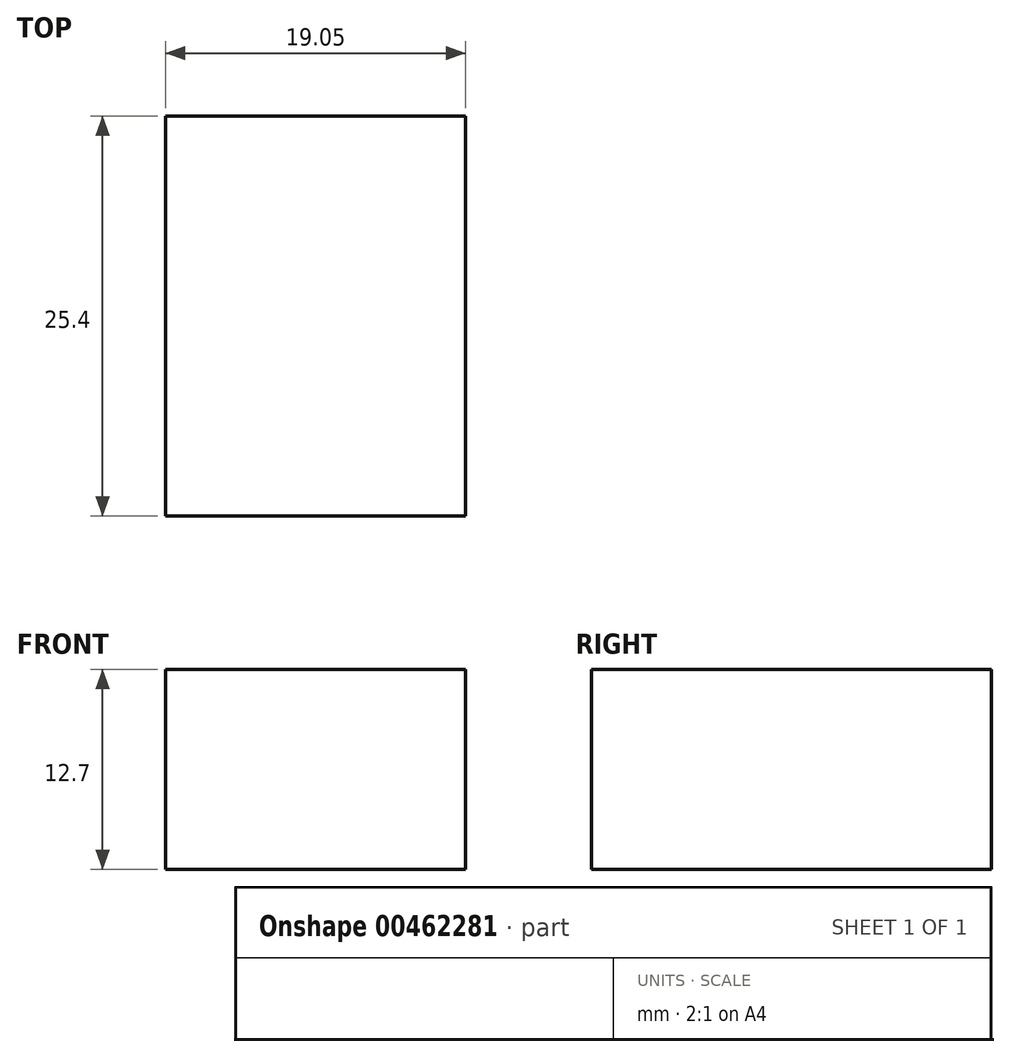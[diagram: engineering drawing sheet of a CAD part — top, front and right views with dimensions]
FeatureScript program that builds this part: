
annotation { "Feature Type Name" : "Feature", "Feature Type Description" : "" }
export const myFeature = defineFeature(function(context is Context, id is Id, definition is map)
    precondition{}
    {
        {
            var Q0;
            Q0=qCreatedBy(makeId("Front.planeOp"),FACE);
            var sketch = newSketch(context, id + "F0", { "sketchPlane" : qUnion([Q0])});
            skLineSegment(sketch, "E0.bottom", {"start": v(-50.8, 25.4) * mm, "end": v(50.8, 25.4) * mm});
            skLineSegment(sketch, "E0.top", {"start": v(-50.8, -25.4) * mm, "end": v(50.8, -25.4) * mm});
            skLineSegment(sketch, "E0.left", {"start": v(-50.8, 25.4) * mm, "end": v(-50.8, -25.4) * mm});
            skLineSegment(sketch, "E0.right", {"start": v(50.8, 25.4) * mm, "end": v(50.8, -25.4) * mm});
            skPoint(sketch, "E0.middle", {"position": v(0, 0) * mm});
            skLineSegment(sketch, "E1.bottom", {"start": v(31.75, -25.4) * mm, "end": v(50.8, -25.4) * mm});
            skLineSegment(sketch, "E1.top", {"start": v(31.75, -12.7) * mm, "end": v(50.8, -12.7) * mm});
            skLineSegment(sketch, "E1.left", {"start": v(31.75, -25.4) * mm, "end": v(31.75, -12.7) * mm});
            skLineSegment(sketch, "E1.right", {"start": v(50.8, -25.4) * mm, "end": v(50.8, -12.7) * mm});
            skLineSegment(sketch, "E2.bottom", {"start": v(-23.76, 25.4) * mm, "end": v(27.04, 25.4) * mm});
            skLineSegment(sketch, "E2.top", {"start": v(-23.76, 12.7) * mm, "end": v(27.04, 12.7) * mm});
            skLineSegment(sketch, "E2.left", {"start": v(-23.76, 25.4) * mm, "end": v(-23.76, 12.7) * mm});
            skLineSegment(sketch, "E2.right", {"start": v(27.04, 25.4) * mm, "end": v(27.04, 12.7) * mm});
            skSolve(sketch);
        }
        {
            var Q0;
            Q0=makeQuery(id+"F0.imprint","IMPRINT",FACE,{"disambiguationData":[TD([[makeQuery(id+"F0.imprint","IMPRINT",EDGE,{"derivedFrom":sQuery(id+"F0.wireOp",EDGE,"E0.top")}),1.0]])]});
            extrude(context, id + "F1", {"entities" : qUnion([Q0]), "depth" : 25.4 * mm});
        }
        {
            var Q0;
            Q0=makeQuery(id+"F1.opExtrude","SWEPT_FACE",FACE,{"disambiguationData":[OSD([sQuery(id+"F0.wireOp",EDGE,"E0.right")])]});
            var sketch = newSketch(context, id + "F2", { "sketchPlane" : qUnion([Q0])});
            skCircle(sketch, "E3", {"center": v(-12.7, 0) * mm, "radius": 6.35 * mm});
            skSolve(sketch);
        }
        {
            var Q0;
            Q0=makeQuery(id+"F2.imprint","IMPRINT",FACE,{"disambiguationData":[TD([[makeQuery(id+"F2.imprint","IMPRINT",EDGE,{"derivedFrom":sQuery(id+"F2.wireOp",EDGE,"E3")}),1.0]])]});
            extrude(context, id + "F3", {"entities" : qUnion([Q0]), "operationType" : NewBodyOperationType.REMOVE, "oppositeDirection" : true, "depth" : 101.6 * mm});
        }
    });
